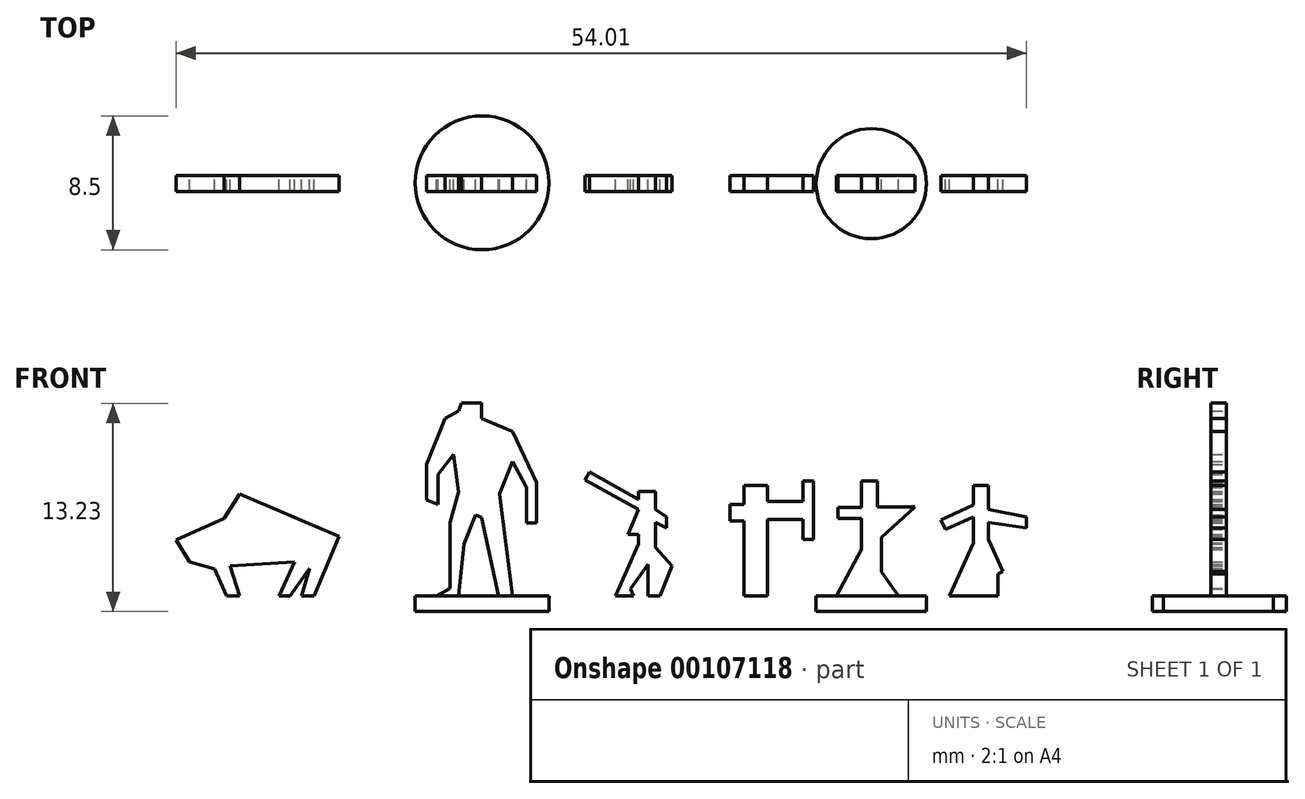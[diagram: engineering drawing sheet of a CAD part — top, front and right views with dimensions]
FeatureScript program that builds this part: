
annotation { "Feature Type Name" : "Feature", "Feature Type Description" : "" }
export const myFeature = defineFeature(function(context is Context, id is Id, definition is map)
    precondition{}
    {
        {
            var Q0;
            Q0=qCreatedBy(makeId("Front.planeOp"),FACE);
            var sketch = newSketch(context, id + "F0", { "sketchPlane" : qUnion([Q0])});
            skLineSegment(sketch, "E0", {"start": v(0, 0) * mm, "end": v(0, 2.93) * mm});
            skLineSegment(sketch, "E1", {"start": v(0, 2.93) * mm, "end": v(0, 4.76) * mm});
            skLineSegment(sketch, "E2", {"start": v(0, 4.76) * mm, "end": v(-0.87, 4.76) * mm});
            skLineSegment(sketch, "E3", {"start": v(-0.87, 4.76) * mm, "end": v(-0.87, 5.8) * mm});
            skLineSegment(sketch, "E4", {"start": v(-0.87, 5.8) * mm, "end": v(0, 5.8) * mm});
            skLineSegment(sketch, "E5", {"start": v(0, 5.8) * mm, "end": v(0, 7) * mm});
            skLineSegment(sketch, "E6", {"start": v(0, 7) * mm, "end": v(1.51, 7) * mm});
            skLineSegment(sketch, "E7", {"start": v(1.51, 7) * mm, "end": v(1.51, 6) * mm});
            skLineSegment(sketch, "E8", {"start": v(1.51, 6) * mm, "end": v(3.75, 6) * mm});
            skLineSegment(sketch, "E9", {"start": v(3.75, 6) * mm, "end": v(3.75, 7.3) * mm});
            skLineSegment(sketch, "E10", {"start": v(3.75, 7.3) * mm, "end": v(4.42, 7.3) * mm});
            skLineSegment(sketch, "E11", {"start": v(4.42, 7.3) * mm, "end": v(4.42, 3.57) * mm});
            skLineSegment(sketch, "E12", {"start": v(4.42, 3.57) * mm, "end": v(3.75, 3.57) * mm});
            skLineSegment(sketch, "E13", {"start": v(3.75, 3.57) * mm, "end": v(3.75, 4.84) * mm});
            skLineSegment(sketch, "E14", {"start": v(3.75, 4.84) * mm, "end": v(1.51, 4.84) * mm});
            skLineSegment(sketch, "E15", {"start": v(1.51, 4.84) * mm, "end": v(1.51, 0) * mm});
            skLineSegment(sketch, "E16", {"start": v(1.51, 0) * mm, "end": v(0, 0) * mm});
            skLineSegment(sketch, "E17", {"start": v(5.87, 0) * mm, "end": v(7.47, 2.93) * mm});
            skLineSegment(sketch, "E18", {"start": v(7.47, 2.93) * mm, "end": v(7.47, 4.91) * mm});
            skLineSegment(sketch, "E19", {"start": v(7.47, 4.91) * mm, "end": v(5.98, 4.91) * mm});
            skLineSegment(sketch, "E20", {"start": v(5.98, 4.91) * mm, "end": v(5.98, 5.62) * mm});
            skLineSegment(sketch, "E21", {"start": v(5.98, 5.62) * mm, "end": v(7.47, 5.62) * mm});
            skLineSegment(sketch, "E22", {"start": v(7.47, 5.62) * mm, "end": v(7.47, 7.3) * mm});
            skLineSegment(sketch, "E23", {"start": v(7.47, 7.3) * mm, "end": v(8.48, 7.3) * mm});
            skLineSegment(sketch, "E24", {"start": v(8.48, 7.3) * mm, "end": v(8.48, 5.66) * mm});
            skLineSegment(sketch, "E25", {"start": v(8.48, 5.66) * mm, "end": v(10.87, 5.66) * mm});
            skLineSegment(sketch, "E26", {"start": v(10.87, 5.66) * mm, "end": v(8.74, 3.72) * mm});
            skLineSegment(sketch, "E27", {"start": v(8.74, 3.72) * mm, "end": v(8.74, 1.51) * mm});
            skLineSegment(sketch, "E28", {"start": v(8.74, 1.51) * mm, "end": v(9.82, 0) * mm});
            skLineSegment(sketch, "E29", {"start": v(9.82, 0) * mm, "end": v(5.87, 0) * mm});
            skLineSegment(sketch, "E30", {"start": v(13.06, 0) * mm, "end": v(14.6, 3.35) * mm});
            skLineSegment(sketch, "E31", {"start": v(14.6, 3.35) * mm, "end": v(14.6, 5.02) * mm});
            skLineSegment(sketch, "E32", {"start": v(14.6, 5.02) * mm, "end": v(12.8, 4.2) * mm});
            skLineSegment(sketch, "E33", {"start": v(12.8, 4.2) * mm, "end": v(12.52, 4.82) * mm});
            skLineSegment(sketch, "E34", {"start": v(12.52, 4.82) * mm, "end": v(14.6, 5.77) * mm});
            skLineSegment(sketch, "E35", {"start": v(14.6, 5.77) * mm, "end": v(14.6, 7) * mm});
            skLineSegment(sketch, "E36", {"start": v(14.6, 7) * mm, "end": v(15.52, 7) * mm});
            skLineSegment(sketch, "E37", {"start": v(15.52, 7) * mm, "end": v(15.52, 5.47) * mm});
            skLineSegment(sketch, "E38", {"start": v(15.52, 5.47) * mm, "end": v(17.95, 5.02) * mm});
            skLineSegment(sketch, "E39", {"start": v(17.95, 5.02) * mm, "end": v(17.95, 4.32) * mm});
            skLineSegment(sketch, "E40", {"start": v(17.95, 4.32) * mm, "end": v(15.52, 4.65) * mm});
            skLineSegment(sketch, "E41", {"start": v(15.52, 4.65) * mm, "end": v(15.52, 3.57) * mm});
            skLineSegment(sketch, "E42", {"start": v(15.52, 3.57) * mm, "end": v(16.45, 1.55) * mm});
            skLineSegment(sketch, "E43", {"start": v(16.45, 1.55) * mm, "end": v(16.13, 1.4) * mm});
            skLineSegment(sketch, "E44", {"start": v(16.13, 1.4) * mm, "end": v(16.13, 0) * mm});
            skLineSegment(sketch, "E45", {"start": v(16.13, 0) * mm, "end": v(13.06, 0) * mm});
            skLineSegment(sketch, "E46", {"start": v(-8.14, 0) * mm, "end": v(-6.69, 3.31) * mm});
            skLineSegment(sketch, "E47", {"start": v(-6.69, 3.31) * mm, "end": v(-6.69, 3.9) * mm});
            skLineSegment(sketch, "E48", {"start": v(-6.69, 3.9) * mm, "end": v(-7.36, 3.9) * mm});
            skLineSegment(sketch, "E49", {"start": v(-7.36, 3.9) * mm, "end": v(-6.69, 5.47) * mm});
            skLineSegment(sketch, "E50", {"start": v(-6.69, 5.47) * mm, "end": v(-10.08, 7.37) * mm});
            skLineSegment(sketch, "E51", {"start": v(-10.08, 7.37) * mm, "end": v(-9.8, 7.87) * mm});
            skLineSegment(sketch, "E52", {"start": v(-9.8, 7.87) * mm, "end": v(-6.69, 6.12) * mm});
            skLineSegment(sketch, "E53", {"start": v(-6.69, 6.12) * mm, "end": v(-6.69, 6.63) * mm});
            skLineSegment(sketch, "E54", {"start": v(-6.69, 6.63) * mm, "end": v(-5.6, 6.63) * mm});
            skLineSegment(sketch, "E55", {"start": v(-5.6, 6.63) * mm, "end": v(-5.6, 6.12) * mm});
            skLineSegment(sketch, "E56", {"start": v(-5.6, 6.12) * mm, "end": v(-5.6, 5.47) * mm});
            skLineSegment(sketch, "E57", {"start": v(-5.6, 5.47) * mm, "end": v(-4.9, 5.02) * mm});
            skLineSegment(sketch, "E58", {"start": v(-4.9, 5.02) * mm, "end": v(-4.9, 4.32) * mm});
            skLineSegment(sketch, "E59", {"start": v(-4.9, 4.32) * mm, "end": v(-5.6, 4.65) * mm});
            skLineSegment(sketch, "E60", {"start": v(-5.6, 4.65) * mm, "end": v(-5.6, 3.09) * mm});
            skLineSegment(sketch, "E61", {"start": v(-5.6, 3.09) * mm, "end": v(-4.56, 1.9) * mm});
            skLineSegment(sketch, "E62", {"start": v(-4.56, 1.9) * mm, "end": v(-5.3, 0) * mm});
            skLineSegment(sketch, "E63", {"start": v(-5.3, 0) * mm, "end": v(-6.1, 0) * mm});
            skLineSegment(sketch, "E64", {"start": v(-6.1, 0) * mm, "end": v(-6.1, 2) * mm});
            skLineSegment(sketch, "E65", {"start": v(-6.1, 2) * mm, "end": v(-7.2, 0.44) * mm});
            skLineSegment(sketch, "E66", {"start": v(-7.2, 0.44) * mm, "end": v(-7, 0) * mm});
            skLineSegment(sketch, "E67", {"start": v(-7, 0) * mm, "end": v(-8.14, 0) * mm});
            skLineSegment(sketch, "E68", {"start": v(-14.68, 0) * mm, "end": v(-15.51, 6.48) * mm});
            skLineSegment(sketch, "E69", {"start": v(-15.51, 6.48) * mm, "end": v(-14.68, 8.55) * mm});
            skLineSegment(sketch, "E70", {"start": v(-14.68, 8.55) * mm, "end": v(-13.78, 6.87) * mm});
            skLineSegment(sketch, "E71", {"start": v(-13.78, 6.87) * mm, "end": v(-13.78, 4.64) * mm});
            skLineSegment(sketch, "E72", {"start": v(-13.78, 4.64) * mm, "end": v(-13.17, 4.64) * mm});
            skLineSegment(sketch, "E73", {"start": v(-13.17, 4.64) * mm, "end": v(-13.17, 7.2) * mm});
            skLineSegment(sketch, "E74", {"start": v(-13.17, 7.2) * mm, "end": v(-14.68, 10.45) * mm});
            skLineSegment(sketch, "E75", {"start": v(-14.68, 10.45) * mm, "end": v(-16.66, 11.25) * mm});
            skLineSegment(sketch, "E76", {"start": v(-16.66, 11.25) * mm, "end": v(-16.66, 12.23) * mm});
            skLineSegment(sketch, "E77", {"start": v(-16.66, 12.23) * mm, "end": v(-17.92, 12.23) * mm});
            skLineSegment(sketch, "E78", {"start": v(-17.92, 12.23) * mm, "end": v(-18.12, 11.73) * mm});
            skLineSegment(sketch, "E79", {"start": v(-18.12, 11.73) * mm, "end": v(-18.98, 11.25) * mm});
            skLineSegment(sketch, "E80", {"start": v(-18.98, 11.25) * mm, "end": v(-20.16, 8.33) * mm});
            skLineSegment(sketch, "E81", {"start": v(-20.16, 8.33) * mm, "end": v(-20.16, 6.1) * mm});
            skLineSegment(sketch, "E82", {"start": v(-20.16, 6.1) * mm, "end": v(-19.43, 5.8) * mm});
            skLineSegment(sketch, "E83", {"start": v(-19.43, 5.8) * mm, "end": v(-19.43, 7.71) * mm});
            skLineSegment(sketch, "E84", {"start": v(-19.43, 7.71) * mm, "end": v(-18.42, 8.97) * mm});
            skLineSegment(sketch, "E85", {"start": v(-18.42, 8.97) * mm, "end": v(-18.12, 6.6) * mm});
            skLineSegment(sketch, "E86", {"start": v(-18.12, 6.6) * mm, "end": v(-18.65, 4.65) * mm});
            skLineSegment(sketch, "E87", {"start": v(-18.65, 4.65) * mm, "end": v(-18.65, 0.48) * mm});
            skLineSegment(sketch, "E88", {"start": v(-18.65, 0.48) * mm, "end": v(-19.51, 0) * mm});
            skLineSegment(sketch, "E89", {"start": v(-19.51, 0) * mm, "end": v(-18.12, 0) * mm});
            skLineSegment(sketch, "E90", {"start": v(-18.12, 0) * mm, "end": v(-17.77, 3.29) * mm});
            skLineSegment(sketch, "E91", {"start": v(-17.77, 3.29) * mm, "end": v(-17.02, 5.13) * mm});
            skLineSegment(sketch, "E92", {"start": v(-17.02, 5.13) * mm, "end": v(-16.66, 4.98) * mm});
            skLineSegment(sketch, "E93", {"start": v(-16.66, 4.98) * mm, "end": v(-15.58, 0) * mm});
            skLineSegment(sketch, "E94", {"start": v(-15.58, 0) * mm, "end": v(-14.68, 0) * mm});
            skLineSegment(sketch, "E95", {"start": v(-33, 4.9) * mm, "end": v(-32.04, 6.46) * mm});
            skLineSegment(sketch, "E96", {"start": v(-32.04, 6.46) * mm, "end": v(-25.7, 3.77) * mm});
            skLineSegment(sketch, "E97", {"start": v(-25.7, 3.77) * mm, "end": v(-27.3, 0) * mm});
            skLineSegment(sketch, "E98", {"start": v(-27.3, 0) * mm, "end": v(-28.1, 0) * mm});
            skLineSegment(sketch, "E99", {"start": v(-28.1, 0) * mm, "end": v(-27.59, 1.74) * mm});
            skLineSegment(sketch, "E100", {"start": v(-27.59, 1.74) * mm, "end": v(-28.82, 0) * mm});
            skLineSegment(sketch, "E101", {"start": v(-28.82, 0) * mm, "end": v(-29.5, 0) * mm});
            skLineSegment(sketch, "E102", {"start": v(-29.5, 0) * mm, "end": v(-28.52, 2.14) * mm});
            skLineSegment(sketch, "E103", {"start": v(-28.52, 2.14) * mm, "end": v(-32.62, 1.89) * mm});
            skLineSegment(sketch, "E104", {"start": v(-32.62, 1.89) * mm, "end": v(-32.02, 0) * mm});
            skLineSegment(sketch, "E105", {"start": v(-32.02, 0) * mm, "end": v(-32.85, 0) * mm});
            skLineSegment(sketch, "E106", {"start": v(-32.85, 0) * mm, "end": v(-33.6, 1.7) * mm});
            skLineSegment(sketch, "E107", {"start": v(-33.6, 1.7) * mm, "end": v(-35.2, 2.14) * mm});
            skLineSegment(sketch, "E108", {"start": v(-35.2, 2.14) * mm, "end": v(-36.06, 3.55) * mm});
            skLineSegment(sketch, "E109", {"start": v(-36.06, 3.55) * mm, "end": v(-33, 4.9) * mm});
            skPoint(sketch, "E110.orphan", {"position": v(-33.97, 3.34) * mm});
            skSolve(sketch);
        }
        {
            var Q0;
            Q0 = qSketchRegion(id + "F0", true);
            extrude(context, id + "F1", {"entities" : qUnion([Q0]), "depth" : 1 * mm});
        }
        {
            var Q0;
            Q0=qCreatedBy(makeId("Top.planeOp"),FACE);
            var sketch = newSketch(context, id + "F2", { "sketchPlane" : qUnion([Q0])});
            skCircle(sketch, "E111", {"center": v(8.1, -0.5) * mm, "radius": 3.5 * mm});
            skCircle(sketch, "E112", {"center": v(-16.62, -0.46) * mm, "radius": 4.25 * mm});
            skSolve(sketch);
        }
        {
            var Q0;
            Q0=makeQuery(id+"F2.imprint","IMPRINT",FACE,{"disambiguationData":[TD([[makeQuery(id+"F2.imprint","IMPRINT",EDGE,{"derivedFrom":sQuery(id+"F2.wireOp",EDGE,"E111")}),1.0]])]});
            extrude(context, id + "F3", {"entities" : qUnion([Q0]), "oppositeDirection" : true, "depth" : 1 * mm});
        }
        {
            var Q0;
            Q0=makeQuery(id+"F2.imprint","IMPRINT",FACE,{"disambiguationData":[TD([[makeQuery(id+"F2.imprint","IMPRINT",EDGE,{"derivedFrom":sQuery(id+"F2.wireOp",EDGE,"E112")}),1.0]])]});
            extrude(context, id + "F4", {"entities" : qUnion([Q0]), "oppositeDirection" : true, "depth" : 1 * mm});
        }
    });
